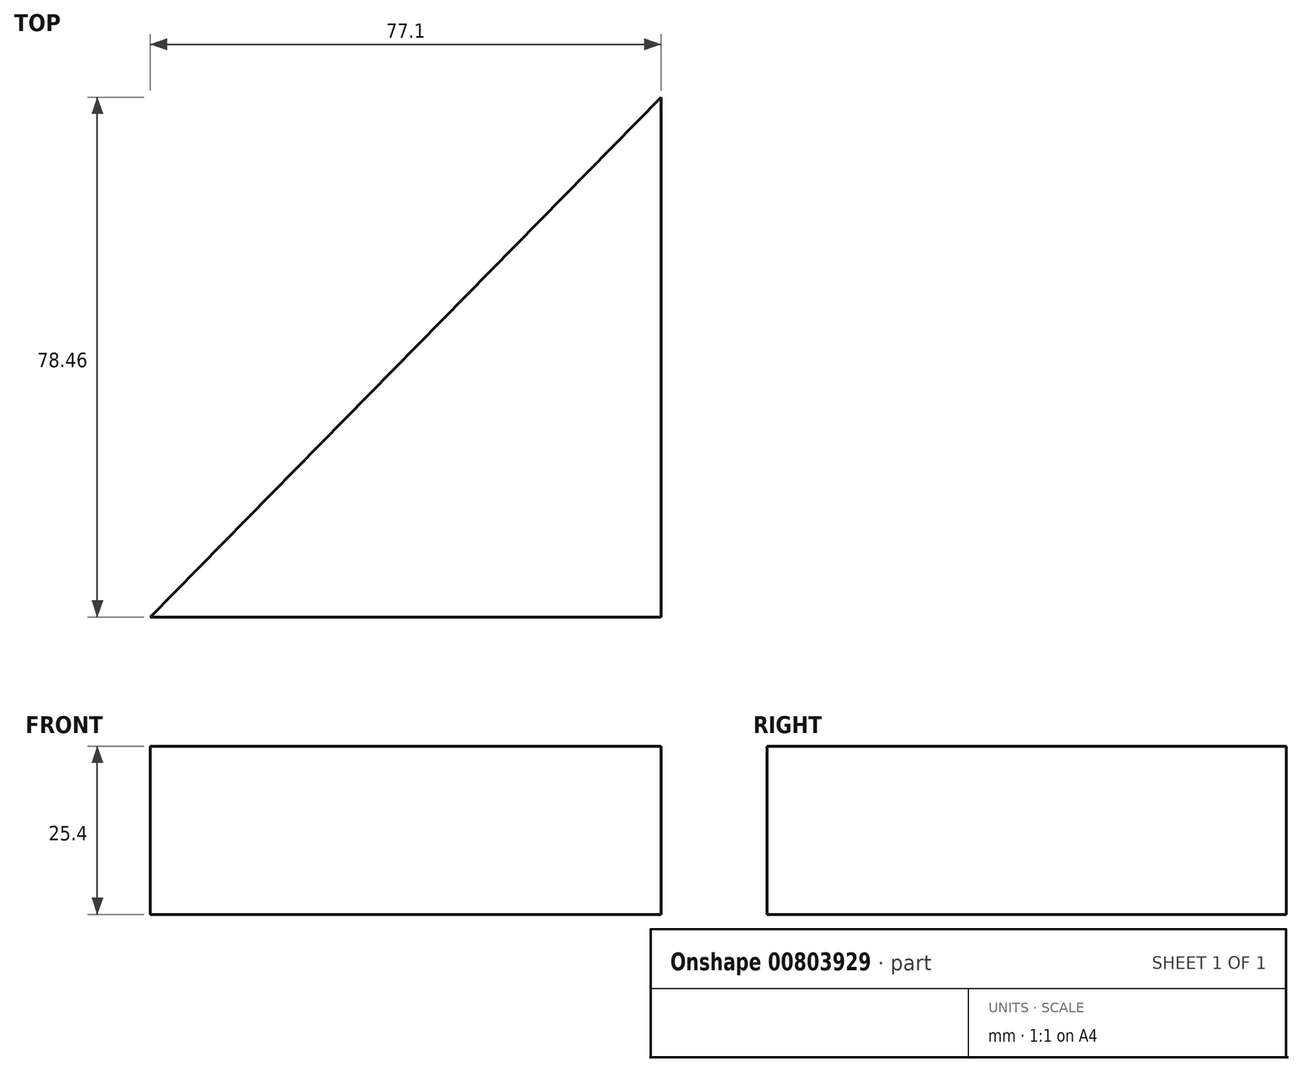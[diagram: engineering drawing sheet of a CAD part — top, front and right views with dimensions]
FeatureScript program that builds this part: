
annotation { "Feature Type Name" : "Feature", "Feature Type Description" : "" }
export const myFeature = defineFeature(function(context is Context, id is Id, definition is map)
    precondition{}
    {
        {
            var Q0;
            Q0=qCreatedBy(makeId("Top.planeOp"),FACE);
            var sketch = newSketch(context, id + "F0", { "sketchPlane" : qUnion([Q0])});
            skLineSegment(sketch, "E0", {"start": v(0, 0) * mm, "end": v(77.1, 0) * mm});
            skLineSegment(sketch, "E1", {"start": v(77.1, 0) * mm, "end": v(77.1, 78.46) * mm});
            skLineSegment(sketch, "E2", {"start": v(77.1, 78.46) * mm, "end": v(0, 0) * mm});
            skSolve(sketch);
        }
        {
            var Q0;
            Q0=makeQuery(id+"F0.imprint","IMPRINT",FACE,{"disambiguationData":[TD([[makeQuery(id+"F0.imprint","IMPRINT",EDGE,{"derivedFrom":sQuery(id+"F0.wireOp",EDGE,"E0")}),1.0]])]});
            extrude(context, id + "F1", {"entities" : qUnion([Q0]), "depth" : 25.4 * mm, "offsetDistance" : 25.4 * mm});
        }
    });
